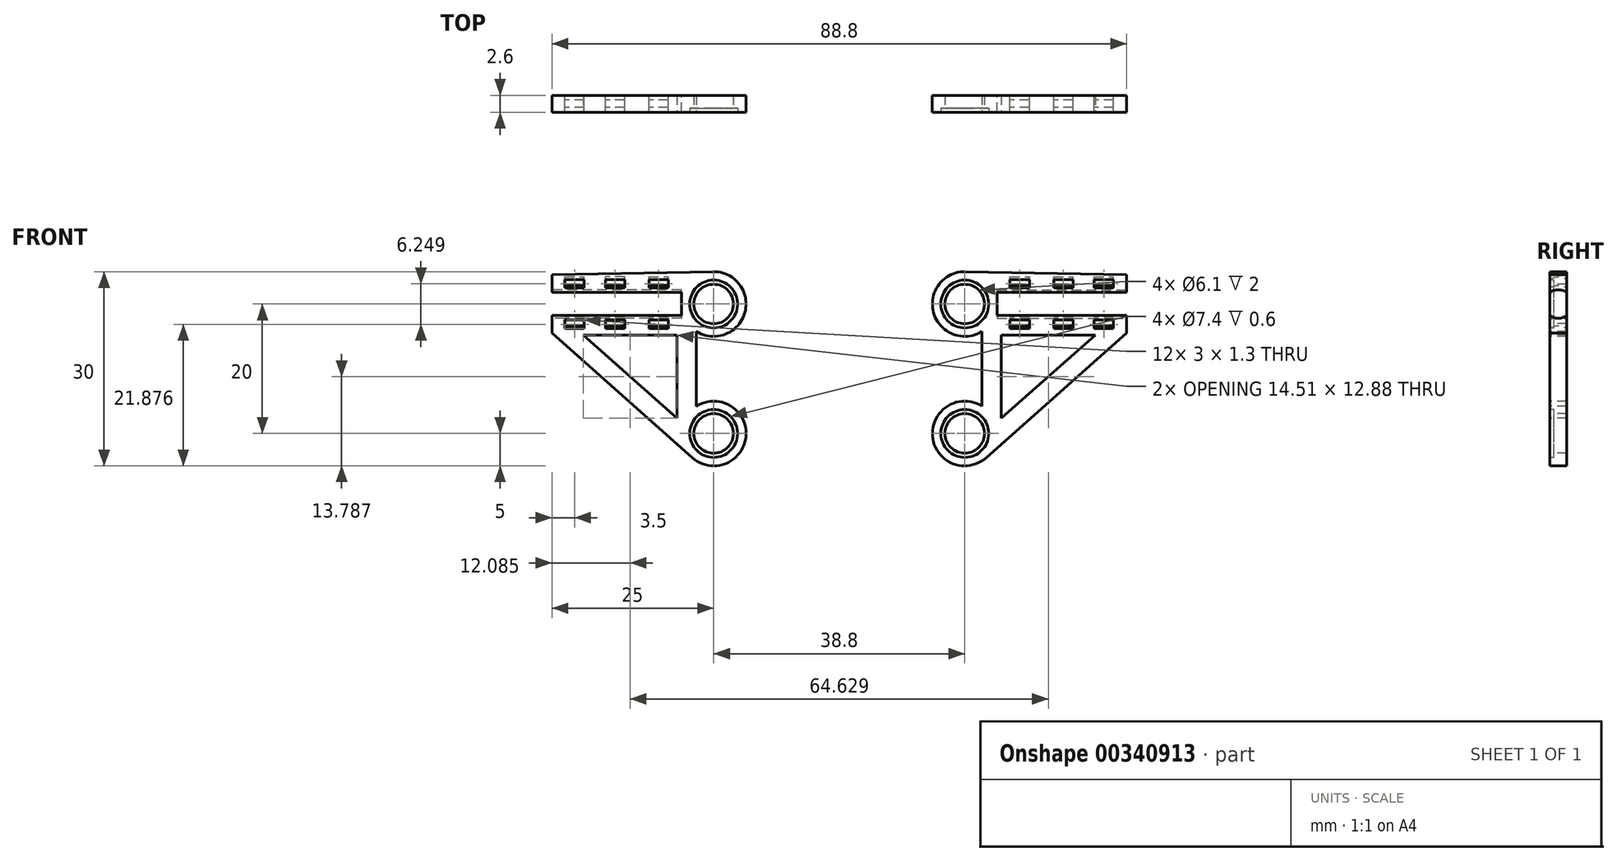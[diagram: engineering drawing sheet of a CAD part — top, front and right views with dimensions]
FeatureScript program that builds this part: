
annotation { "Feature Type Name" : "Feature", "Feature Type Description" : "" }
export const myFeature = defineFeature(function(context is Context, id is Id, definition is map)
    precondition{}
    {
        {
            var Q0;
            Q0=qCreatedBy(makeId("Front.planeOp"),FACE);
            var sketch = newSketch(context, id + "F0", { "sketchPlane" : qUnion([Q0])});
            skLineSegment(sketch, "E0", {"start": v(0.1, 5) * mm, "end": v(25, 4.5) * mm});
            skLineSegment(sketch, "E1", {"start": v(25, 4.5) * mm, "end": v(25, -4.5) * mm});
            skLineSegment(sketch, "E2", {"start": v(25, -4.5) * mm, "end": v(3.32, -23.74) * mm});
            skPoint(sketch, "E3", {"position": v(0, 0) * mm});
            skPoint(sketch, "E4", {"position": v(0, -20) * mm});
            skLineSegment(sketch, "E5", {"start": v(0, 0) * mm, "end": v(25, 0) * mm, "construction": true});
            skArc(sketch, "E6.filletArc", {"start": v(2.66, -15.77) * mm, "mid": v(-4.98, -20.41) * mm, "end": v(3.32, -23.74) * mm});
            skArc(sketch, "E7.filletArc", {"start": v(0.1, 5) * mm, "mid": v(-4.82, -1.34) * mm, "end": v(2.66, -4.23) * mm});
            skLineSegment(sketch, "E8", {"start": v(2.66, -4.23) * mm, "end": v(2.66, -15.77) * mm});
            skSolve(sketch);
        }
        {
            var Q0;
            Q0=makeQuery(id+"F0.imprint","IMPRINT",FACE,{"disambiguationData":[TD([[makeQuery(id+"F0.imprint","IMPRINT",EDGE,{"derivedFrom":sQuery(id+"F0.wireOp",EDGE,"E0")}),-1.0]])]});
            extrude(context, id + "F1", {"entities" : qUnion([Q0]), "oppositeDirection" : true, "depth" : 2.6 * mm, "offsetDistance" : 25 * mm});
        }
        {
            var Q0;
            Q0=sQuery(id+"F0.wireOp",VERTEX,"E3");
            var Q1;
            Q1=sQuery(id+"F0.wireOp",VERTEX,"E4");
            var Q2;
            Q2=makeQuery(id+"F1.opExtrude","SWEPT_BODY",BODY,{"disambiguationData":[OSD([sQuery(id+"F0.wireOp",EDGE,"RJbdalpD-36lB-MyLH-ccrA-Tx8w9Rtr1OP7"),sQuery(id+"F0.wireOp",EDGE,"E0"),sQuery(id+"F0.wireOp",EDGE,"E1"),sQuery(id+"F0.wireOp",EDGE,"E2"),sQuery(id+"F0.wireOp",EDGE,"E6.filletArc"),sQuery(id+"F0.wireOp",EDGE,"E7.filletArc")])]});
            hole(context, id + "F2", {"style" : HoleStyle.C_BORE, "endStyle" : HoleEndStyle.BLIND, "holeDiameter" : 6.1 * mm, "cBoreDiameter" : 7.4 * mm, "cBoreDepth" : 0.6 * mm, "majorDiameter" : 5 * mm, "holeDepth" : 3 * mm, "isTappedThrough" : true, "tappedDepth" : 12 * mm, "tapClearance" : 3, "startFromSketch" : true, "locations" : qUnion([Q0, Q1]), "scope" : qUnion([Q2])});
        }
        {
            var Q0;
            Q0=makeQuery(id+"F1.opExtrude","SWEPT_FACE",FACE,{"disambiguationData":[OSD([sQuery(id+"F0.wireOp",EDGE,"E1")])]});
            var sketch = newSketch(context, id + "F3", { "sketchPlane" : qUnion([Q0])});
            skCircle(sketch, "E9", {"center": v(1.3, 0) * mm, "radius": 2.2 * mm});
            skPoint(sketch, "E9.centerSnap0", {"position": v(1.3, 4.5) * mm});
            skPoint(sketch, "E9.centerSnap1", {"position": v(2.6, 0) * mm});
            skSolve(sketch);
        }
        {
            var Q0;
            Q0 = qSketchRegion(id + "F3", true);
            extrude(context, id + "F4", {"entities" : qUnion([Q0]), "operationType" : NewBodyOperationType.REMOVE, "oppositeDirection" : true, "depth" : 20 * mm, "offsetDistance" : 25 * mm});
        }
        {
            var Q0;
            Q0=qCreatedBy(makeId("Front.planeOp"),FACE);
            var sketch = newSketch(context, id + "F5", { "sketchPlane" : qUnion([Q0])});
            skLineSegment(sketch, "E10", {"start": v(5.66, -4.77) * mm, "end": v(5.66, -17.65) * mm});
            skLineSegment(sketch, "E11", {"start": v(5.66, -17.65) * mm, "end": v(20.17, -4.77) * mm});
            skLineSegment(sketch, "E12", {"start": v(20.17, -4.77) * mm, "end": v(5.66, -4.77) * mm});
            skSolve(sketch);
        }
        {
            var Q0;
            Q0 = qSketchRegion(id + "F5", true);
            extrude(context, id + "F6", {"entities" : qUnion([Q0]), "operationType" : NewBodyOperationType.REMOVE, "oppositeDirection" : true, "depth" : 25 * mm, "offsetDistance" : 25 * mm});
        }
        {
            var Q0;
            Q0=makeQuery(id+"F1.opExtrude","CAP_FACE",FACE,{"disambiguationData":[OSD([sQuery(id+"F0.wireOp",EDGE,"E0"),sQuery(id+"F0.wireOp",EDGE,"E1"),sQuery(id+"F0.wireOp",EDGE,"E2"),sQuery(id+"F0.wireOp",EDGE,"E6.filletArc"),sQuery(id+"F0.wireOp",EDGE,"E7.filletArc"),sQuery(id+"F0.wireOp",EDGE,"E8")])],"isStart":true});
            var sketch = newSketch(context, id + "F7", { "sketchPlane" : qUnion([Q0])});
            skLineSegment(sketch, "E13.bottom", {"start": v(20, 3.77) * mm, "end": v(23, 3.77) * mm});
            skLineSegment(sketch, "E13.top", {"start": v(20, 2.47) * mm, "end": v(23, 2.47) * mm});
            skLineSegment(sketch, "E13.left", {"start": v(20, 3.77) * mm, "end": v(20, 2.47) * mm});
            skLineSegment(sketch, "E13.right", {"start": v(23, 3.77) * mm, "end": v(23, 2.47) * mm});
            skLineSegment(sketch, "E14.bottom", {"start": v(7, 3.77) * mm, "end": v(10, 3.77) * mm});
            skLineSegment(sketch, "E14.top", {"start": v(7, 2.47) * mm, "end": v(10, 2.47) * mm});
            skLineSegment(sketch, "E14.left", {"start": v(7, 3.77) * mm, "end": v(7, 2.47) * mm});
            skLineSegment(sketch, "E14.right", {"start": v(10, 3.77) * mm, "end": v(10, 2.47) * mm});
            skLineSegment(sketch, "E15.bottom", {"start": v(7, -2.47) * mm, "end": v(10, -2.47) * mm});
            skLineSegment(sketch, "E15.top", {"start": v(7, -3.77) * mm, "end": v(10, -3.77) * mm});
            skLineSegment(sketch, "E15.left", {"start": v(7, -2.47) * mm, "end": v(7, -3.77) * mm});
            skLineSegment(sketch, "E15.right", {"start": v(10, -2.47) * mm, "end": v(10, -3.77) * mm});
            skLineSegment(sketch, "E16.bottom", {"start": v(20, -2.47) * mm, "end": v(23, -2.47) * mm});
            skLineSegment(sketch, "E16.top", {"start": v(20, -3.77) * mm, "end": v(23, -3.77) * mm});
            skLineSegment(sketch, "E16.left", {"start": v(20, -2.47) * mm, "end": v(20, -3.77) * mm});
            skLineSegment(sketch, "E16.right", {"start": v(23, -2.47) * mm, "end": v(23, -3.77) * mm});
            skLineSegment(sketch, "E17.bottom", {"start": v(13.74, 3.77) * mm, "end": v(16.74, 3.77) * mm});
            skLineSegment(sketch, "E17.top", {"start": v(13.74, 2.47) * mm, "end": v(16.74, 2.47) * mm});
            skLineSegment(sketch, "E17.left", {"start": v(13.74, 3.77) * mm, "end": v(13.74, 2.47) * mm});
            skLineSegment(sketch, "E17.right", {"start": v(16.74, 3.77) * mm, "end": v(16.74, 2.47) * mm});
            skLineSegment(sketch, "E18.bottom", {"start": v(13.74, -2.47) * mm, "end": v(16.74, -2.47) * mm});
            skLineSegment(sketch, "E18.top", {"start": v(13.74, -3.77) * mm, "end": v(16.74, -3.77) * mm});
            skLineSegment(sketch, "E18.left", {"start": v(13.74, -2.47) * mm, "end": v(13.74, -3.77) * mm});
            skLineSegment(sketch, "E18.right", {"start": v(16.74, -2.47) * mm, "end": v(16.74, -3.77) * mm});
            skSolve(sketch);
        }
        {
            var Q0;
            Q0=makeQuery(id+"F7.imprint","IMPRINT",FACE,{"disambiguationData":[TD([[makeQuery(id+"F7.imprint","IMPRINT",EDGE,{"derivedFrom":sQuery(id+"F7.wireOp",EDGE,"E14.bottom")}),-1.0]])]});
            var Q1;
            Q1=makeQuery(id+"F7.imprint","IMPRINT",FACE,{"disambiguationData":[TD([[makeQuery(id+"F7.imprint","IMPRINT",EDGE,{"derivedFrom":sQuery(id+"F7.wireOp",EDGE,"E17.bottom")}),-1.0]])]});
            var Q2;
            Q2=makeQuery(id+"F7.imprint","IMPRINT",FACE,{"disambiguationData":[TD([[makeQuery(id+"F7.imprint","IMPRINT",EDGE,{"derivedFrom":sQuery(id+"F7.wireOp",EDGE,"E13.bottom")}),-1.0]])]});
            var Q3;
            Q3=makeQuery(id+"F4.boolean.opBoolean","COPY",EDGE,{"disambiguationData":[OD(0.0)],"derivedFrom":makeQuery(id+"F4.opExtrude","CAP_EDGE",EDGE,{"disambiguationData":[OSD([sQuery(id+"F3.wireOp",EDGE,"E9")])],"isStart":true})});
            sweep(context, id + "F8", {"operationType" : NewBodyOperationType.REMOVE, "profiles" : qUnion([Q0, Q1, Q2]), "path" : qUnion([Q3]), "keepProfileOrientation" : true});
        }
        {
            var Q0;
            Q0=makeQuery(id+"F7.imprint","IMPRINT",FACE,{"disambiguationData":[TD([[makeQuery(id+"F7.imprint","IMPRINT",EDGE,{"derivedFrom":sQuery(id+"F7.wireOp",EDGE,"E15.bottom")}),-1.0]])]});
            var Q1;
            Q1=makeQuery(id+"F7.imprint","IMPRINT",FACE,{"disambiguationData":[TD([[makeQuery(id+"F7.imprint","IMPRINT",EDGE,{"derivedFrom":sQuery(id+"F7.wireOp",EDGE,"E18.bottom")}),-1.0]])]});
            var Q2;
            Q2=makeQuery(id+"F7.imprint","IMPRINT",FACE,{"disambiguationData":[TD([[makeQuery(id+"F7.imprint","IMPRINT",EDGE,{"derivedFrom":sQuery(id+"F7.wireOp",EDGE,"E16.bottom")}),-1.0]])]});
            var Q3;
            Q3=makeQuery(id+"F4.boolean.opBoolean","COPY",EDGE,{"disambiguationData":[OD(1.0)],"derivedFrom":makeQuery(id+"F4.opExtrude","CAP_EDGE",EDGE,{"disambiguationData":[OSD([sQuery(id+"F3.wireOp",EDGE,"E9")])],"isStart":true})});
            sweep(context, id + "F9", {"operationType" : NewBodyOperationType.REMOVE, "profiles" : qUnion([Q0, Q1, Q2]), "path" : qUnion([Q3]), "keepProfileOrientation" : true});
        }
        {
            var Q0;
            Q0=qCreatedBy(makeId("Right.planeOp"),FACE);
            cPlane(context, id + "F10", {"entities" : qUnion([Q0]), "cplaneType" : CPlaneType.OFFSET, "offset" : 19.4 * mm, "oppositeDirection" : true, "width" : 150 * mm, "height" : 150 * mm});
        }
        {
            var Q0;
            Q0=makeQuery(id+"F1.opExtrude","SWEPT_BODY",BODY,{"disambiguationData":[OSD([sQuery(id+"F0.wireOp",EDGE,"RJbdalpD-36lB-MyLH-ccrA-Tx8w9Rtr1OP7"),sQuery(id+"F0.wireOp",EDGE,"E0"),sQuery(id+"F0.wireOp",EDGE,"E1"),sQuery(id+"F0.wireOp",EDGE,"E2"),sQuery(id+"F0.wireOp",EDGE,"E6.filletArc"),sQuery(id+"F0.wireOp",EDGE,"E7.filletArc")])]});
            var Q1;
            Q1=qCreatedBy(id+"F10.planeOp",FACE);
            mirror(context, id + "F11", {"entities" : qUnion([Q0]), "mirrorPlane" : qUnion([Q1])});
        }
    });
